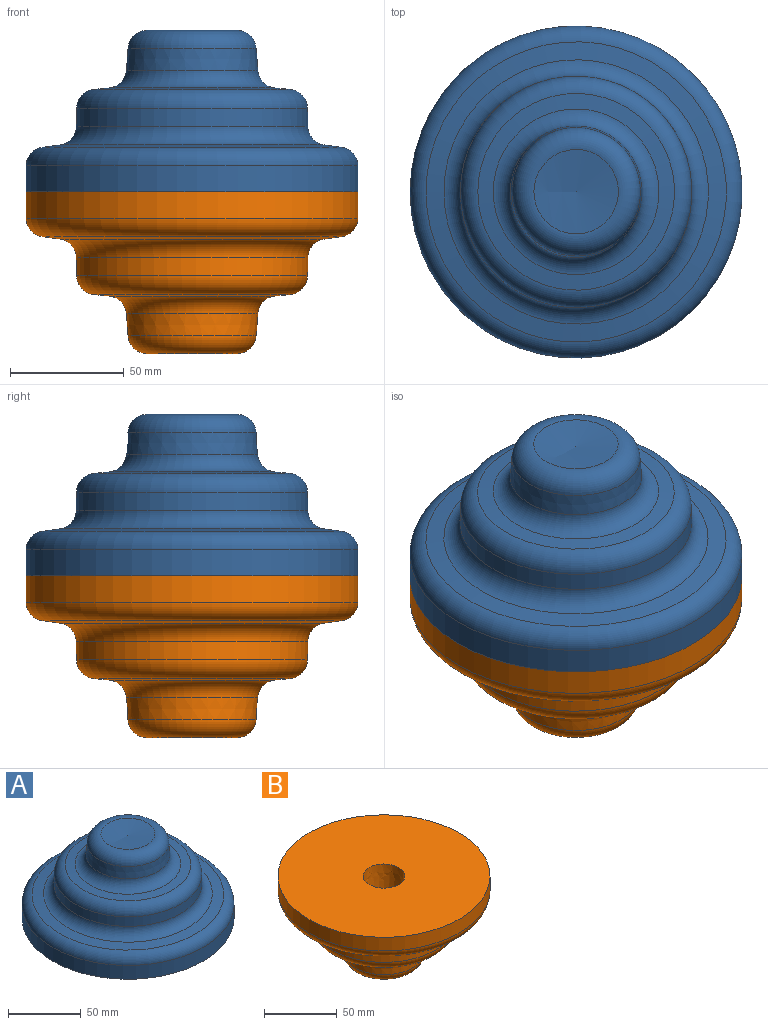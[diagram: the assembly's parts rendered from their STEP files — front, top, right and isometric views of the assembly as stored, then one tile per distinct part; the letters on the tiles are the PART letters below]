
ASSEMBLY  parts=2 mates=1
PART A: 23 faces, bbox 158.1x158.1x71.1 mm
  f0: torus R=37.25mm, axis (0,0,-1), area 2338.2mm2, adj f1,f11
  f1: cone r=28.89mm half-angle=4.1deg, axis (0,0,-1), area 1757.2mm2, adj f0,f2
  f2: torus R=19.83mm, axis (0,0,-1), area 2127mm2, adj f1,f3
  f3: sphere r=124.24mm, area 1090.1mm2, adj f2
  f4: cone r=0mm half-angle=89.8deg, axis (0,0,-1), area 1145.2mm2, adj f5,f16
  f5: cylinder r=73.03mm len=146.05mm, axis (0,0,-1), area 5302.7mm2, adj f4,f6
  f6: torus R=64.9mm, axis (0,0,-1), area 5150.5mm2, adj f5,f7
  f7: cone r=58.13mm half-angle=81.9deg, axis (0,0,-1), area 3117.2mm2, adj f6,f8
  f8: torus R=59.3mm, axis (0,0,-1), area 3988.7mm2, adj f7,f9
  f9: cone r=50.92mm half-angle=0.9deg, axis (0,0,-1), area 2548.3mm2, adj f8,f10
  f10: torus R=42.42mm, axis (0,0,-1), area 3685.9mm2, adj f9,f11
  f11: cone r=36.42mm half-angle=84.3deg, axis (0,0,-1), area 1718.6mm2, adj f0,f10
  f12: torus R=37.25mm, axis (0,0,-1), area 2885.7mm2, adj f13,f22
  f13: cone r=26.36mm half-angle=4.1deg, axis (0,0,-1), area 1601.2mm2, adj f12,f14
  f14: torus R=19.83mm, axis (0,0,-1), area 1397mm2, adj f13,f15
  f15: sphere r=126.78mm, area 1135.2mm2, adj f14
  f16: cylinder r=70.48mm len=140.97mm, axis (0,0,-1), area 5114.7mm2, adj f4,f17
  f17: torus R=64.9mm, axis (0,0,-1), area 3452.7mm2, adj f16,f18
  f18: cone r=57.77mm half-angle=81.9deg, axis (0,0,-1), area 3099.3mm2, adj f17,f19
  f19: torus R=59.3mm, axis (0,0,-1), area 5027.4mm2, adj f18,f20
  f20: cone r=48.38mm half-angle=0.9deg, axis (0,0,-1), area 2421.1mm2, adj f19,f21
  f21: torus R=42.42mm, axis (0,0,-1), area 2477.6mm2, adj f20,f22
  f22: cone r=36.17mm half-angle=84.3deg, axis (0,0,-1), area 1707.7mm2, adj f12,f21
PART B: 14 faces, bbox 158.1x158.1x71.1 mm
  f0: plane 15.68x15.68mm, normal (0,0,1), area 193.1mm2, adj f13
  f1: sphere r=124.24mm, area 1090.1mm2, adj f2
  f2: torus R=19.83mm, axis (0,0,-1), area 2127mm2, adj f1,f3
  f3: cone r=28.89mm half-angle=4.1deg, axis (0,0,1), area 1757.2mm2, adj f2,f4
  f4: torus R=37.25mm, axis (0,0,-1), area 2338.2mm2, adj f3,f5
  f5: cone r=36.42mm half-angle=84.3deg, axis (0,0,1), area 1718.6mm2, adj f4,f6
  f6: torus R=42.42mm, axis (0,0,-1), area 3685.9mm2, adj f5,f7
  f7: cone r=50.92mm half-angle=0.9deg, axis (0,0,1), area 2548.3mm2, adj f6,f8
  f8: torus R=59.3mm, axis (0,0,-1), area 3988.7mm2, adj f7,f9
  f9: cone r=58.13mm half-angle=81.9deg, axis (0,0,1), area 3117.2mm2, adj f8,f10
  f10: torus R=64.9mm, axis (0,0,-1), area 5150.5mm2, adj f9,f11
  f11: cylinder r=73.03mm len=146.05mm, axis (0,0,-1), area 5302.7mm2, adj f10,f12
  f12: plane 146.05x146.05mm, normal (0,0,1), area 16101.9mm2, adj f11,f13
  f13: revolved ~53.8x28.79mm, area 4100.4mm2, adj f0,f12
PLACE A t=(0,0,71.2)mm
PLACE B t=(0,0,75.06)mm
MATE slider B.f2 <-> A.f0  axis (0,0,1) through (0,0,70.97)mm
